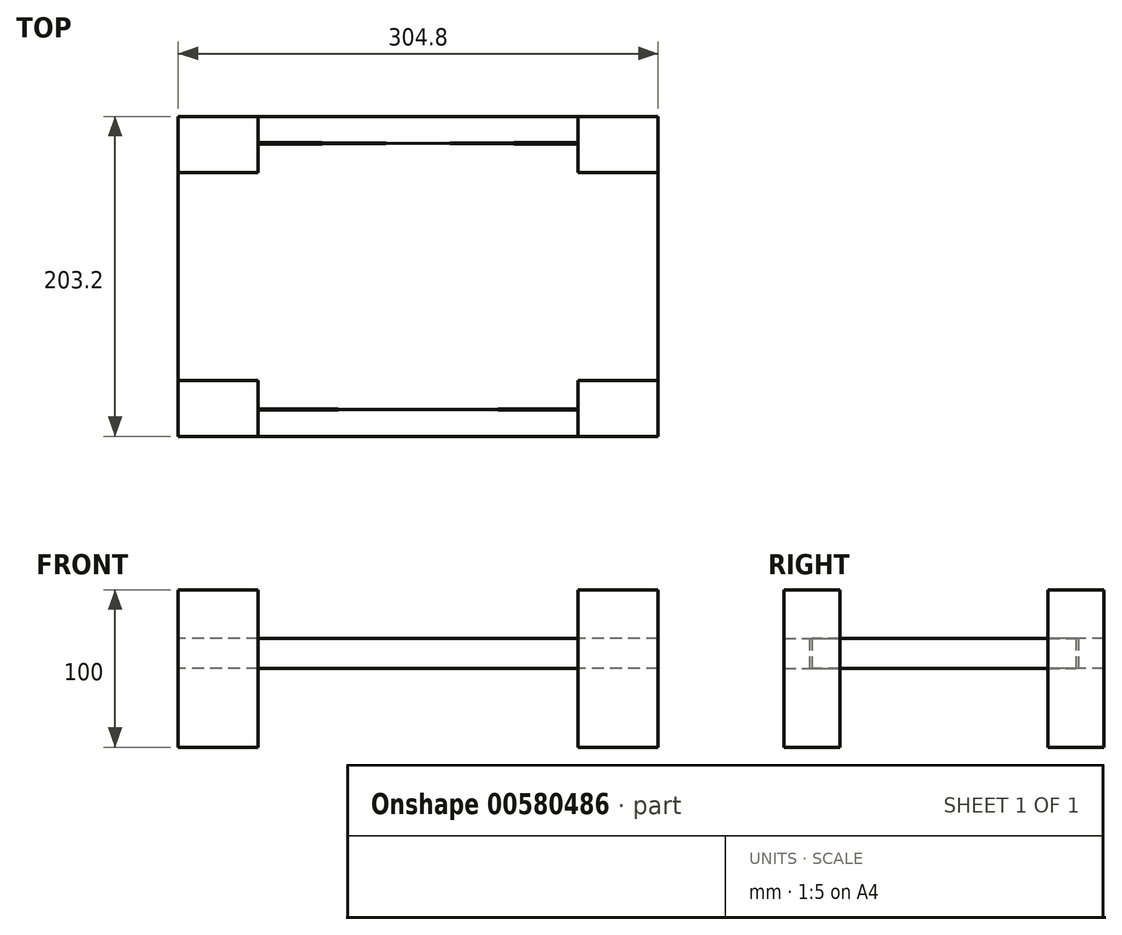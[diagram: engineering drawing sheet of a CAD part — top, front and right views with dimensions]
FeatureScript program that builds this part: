
annotation { "Feature Type Name" : "Feature", "Feature Type Description" : "" }
export const myFeature = defineFeature(function(context is Context, id is Id, definition is map)
    precondition{}
    {
        {
            var Q0;
            Q0=qCreatedBy(makeId("Top.planeOp"),FACE);
            var sketch = newSketch(context, id + "F0", { "sketchPlane" : qUnion([Q0])});
            skLineSegment(sketch, "E0.bottom", {"start": v(152.4, -101.6) * mm, "end": v(-152.4, -101.6) * mm});
            skLineSegment(sketch, "E0.top", {"start": v(152.4, 101.6) * mm, "end": v(-152.4, 101.6) * mm});
            skLineSegment(sketch, "E0.left", {"start": v(152.4, -101.6) * mm, "end": v(152.4, 101.6) * mm});
            skLineSegment(sketch, "E0.right", {"start": v(-152.4, -101.6) * mm, "end": v(-152.4, 101.6) * mm});
            skPoint(sketch, "E0.middle", {"position": v(0, 0) * mm});
            skLineSegment(sketch, "E1.bottom", {"start": v(152.4, -10.16) * mm, "end": v(-152.4, -10.16) * mm});
            skLineSegment(sketch, "E1.top", {"start": v(152.4, 10.16) * mm, "end": v(-152.4, 10.16) * mm});
            skLineSegment(sketch, "E1.left", {"start": v(152.4, -10.16) * mm, "end": v(152.4, 10.16) * mm});
            skLineSegment(sketch, "E1.right", {"start": v(-152.4, -10.16) * mm, "end": v(-152.4, 10.16) * mm});
            skLineSegment(sketch, "E2.bottom", {"start": v(-152.4, 101.6) * mm, "end": v(-101.6, 101.6) * mm});
            skLineSegment(sketch, "E2.top", {"start": v(-152.4, 66.04) * mm, "end": v(-101.6, 66.04) * mm});
            skLineSegment(sketch, "E2.left", {"start": v(-152.4, 101.6) * mm, "end": v(-152.4, 66.04) * mm});
            skLineSegment(sketch, "E2.right", {"start": v(-101.6, 101.6) * mm, "end": v(-101.6, 66.04) * mm});
            skLineSegment(sketch, "E3.MirrorCS", {"start": v(101.6, 101.6) * mm, "end": v(101.6, 66.04) * mm});
            skLineSegment(sketch, "E4.MirrorCS", {"start": v(152.4, 101.6) * mm, "end": v(152.4, 66.04) * mm});
            skLineSegment(sketch, "E5.MirrorCS", {"start": v(152.4, 66.04) * mm, "end": v(101.6, 66.04) * mm});
            skLineSegment(sketch, "E6.MirrorCS", {"start": v(152.4, 101.6) * mm, "end": v(101.6, 101.6) * mm});
            skLineSegment(sketch, "E7.MirrorCS", {"start": v(101.6, -101.6) * mm, "end": v(101.6, -66.04) * mm});
            skLineSegment(sketch, "E8.MirrorCS", {"start": v(-101.6, -101.6) * mm, "end": v(-101.6, -66.04) * mm});
            skLineSegment(sketch, "E9.MirrorCS", {"start": v(-152.4, -101.6) * mm, "end": v(-152.4, -66.04) * mm});
            skLineSegment(sketch, "E10.MirrorCS", {"start": v(-152.4, -66.04) * mm, "end": v(-101.6, -66.04) * mm});
            skLineSegment(sketch, "E11.MirrorCS", {"start": v(152.4, -101.6) * mm, "end": v(152.4, -66.04) * mm});
            skLineSegment(sketch, "E12.MirrorCS", {"start": v(-152.4, -101.6) * mm, "end": v(-101.6, -101.6) * mm});
            skLineSegment(sketch, "E13.MirrorCS", {"start": v(152.4, -66.04) * mm, "end": v(101.6, -66.04) * mm});
            skLineSegment(sketch, "E14.MirrorCS", {"start": v(152.4, -101.6) * mm, "end": v(101.6, -101.6) * mm});
            skLineSegment(sketch, "E15.bottom", {"start": v(-101.6, 101.6) * mm, "end": v(101.6, 101.6) * mm});
            skLineSegment(sketch, "E15.top", {"start": v(-101.6, 85.34) * mm, "end": v(101.6, 83.82) * mm});
            skLineSegment(sketch, "E15.left", {"start": v(-101.6, 101.6) * mm, "end": v(-101.6, 85.34) * mm});
            skLineSegment(sketch, "E15.right", {"start": v(101.6, 101.6) * mm, "end": v(101.6, 83.82) * mm});
            skLineSegment(sketch, "E16.MirrorCS", {"start": v(-101.6, -85.34) * mm, "end": v(101.6, -83.82) * mm});
            skSolve(sketch);
        }
        {
            var Q0;
            Q0=makeQuery(id+"F0.imprint","IMPRINT",FACE,{"disambiguationData":[TD([[makeQuery(id+"F0.imprint","IMPRINT",EDGE,{"derivedFrom":sQuery(id+"F0.wireOp",EDGE,"E1.bottom")}),-1.0]])]});
            var Q1;
            {var subQ1=sQuery(id+"F0.wireOp",EDGE,"E1.top");Q1=makeQuery(id+"F0.imprint","IMPRINT",FACE,{"disambiguationData":[TD([[makeQuery(id+"F0.imprint","IMPRINT",EDGE,{"derivedFrom":subQ1}),-1.0]])]});}
            var Q2;
            {var subQ3=sQuery(id+"F0.wireOp",EDGE,"E16.MirrorCS");Q2=makeQuery(id+"F0.imprint","IMPRINT",FACE,{"disambiguationData":[TD([[makeQuery(id+"F0.imprint","IMPRINT",EDGE,{"derivedFrom":subQ3}),-1.0]])]});}
            var Q3;
            Q3=makeQuery(id+"F0.imprint","IMPRINT",FACE,{"disambiguationData":[TD([[makeQuery(id+"F0.imprint","IMPRINT",EDGE,{"derivedFrom":sQuery(id+"F0.wireOp",EDGE,"E15.bottom")}),-1.0]])]});
            var Q4;
            {var subQ0=sQuery(id+"F0.wireOp",EDGE,"E1.bottom");Q4=makeQuery(id+"F0.imprint","IMPRINT",FACE,{"disambiguationData":[TD([[makeQuery(id+"F0.imprint","IMPRINT",EDGE,{"derivedFrom":subQ0}),1.0]])]});}
            var Q5;
            Q5=makeQuery(id+"F0.imprint","IMPRINT",FACE,{"disambiguationData":[TD([[makeQuery(id+"F0.imprint","IMPRINT",EDGE,{"derivedFrom":sQuery(id+"F0.wireOp",EDGE,"E2.bottom")}),-1.0]])]});
            var Q6;
            {var subQ1=sQuery(id+"F0.wireOp",EDGE,"E9.MirrorCS");Q6=makeQuery(id+"F0.imprint","IMPRINT",FACE,{"disambiguationData":[TD([[makeQuery(id+"F0.imprint","IMPRINT",EDGE,{"derivedFrom":subQ1}),-1.0]])]});}
            var Q7;
            {var subQ1=sQuery(id+"F0.wireOp",EDGE,"E11.MirrorCS");Q7=makeQuery(id+"F0.imprint","IMPRINT",FACE,{"disambiguationData":[TD([[makeQuery(id+"F0.imprint","IMPRINT",EDGE,{"derivedFrom":subQ1}),1.0]])]});}
            var Q8;
            Q8=makeQuery(id+"F0.imprint","IMPRINT",FACE,{"disambiguationData":[TD([[makeQuery(id+"F0.imprint","IMPRINT",EDGE,{"derivedFrom":sQuery(id+"F0.wireOp",EDGE,"E3.MirrorCS")}),1.0]])]});
            extrude(context, id + "F1", {"entities" : qUnion([Q0, Q1, Q2, Q3, Q4, Q5, Q6, Q7, Q8]), "depth" : 19.05 * mm, "offsetDistance" : 25 * mm});
        }
        {
            var Q0;
            {var subQ0=sQuery(id+"F0.wireOp",EDGE,"E8.MirrorCS");Q0=makeQuery(id+"F0.imprint","IMPRINT",FACE,{"disambiguationData":[TD([[makeQuery(id+"F0.imprint","IMPRINT",EDGE,{"derivedFrom":subQ0}),1.0]])]});}
            var Q1;
            Q1=makeQuery(id+"F0.imprint","IMPRINT",FACE,{"disambiguationData":[TD([[makeQuery(id+"F0.imprint","IMPRINT",EDGE,{"derivedFrom":sQuery(id+"F0.wireOp",EDGE,"E2.bottom")}),-1.0]])]});
            var Q2;
            Q2=makeQuery(id+"F0.imprint","IMPRINT",FACE,{"disambiguationData":[TD([[makeQuery(id+"F0.imprint","IMPRINT",EDGE,{"derivedFrom":sQuery(id+"F0.wireOp",EDGE,"E3.MirrorCS")}),1.0]])]});
            var Q3;
            {var subQ0=sQuery(id+"F0.wireOp",EDGE,"E7.MirrorCS");Q3=makeQuery(id+"F0.imprint","IMPRINT",FACE,{"disambiguationData":[TD([[makeQuery(id+"F0.imprint","IMPRINT",EDGE,{"derivedFrom":subQ0}),-1.0]])]});}
            extrude(context, id + "F2", {"entities" : qUnion([Q0, Q1, Q2, Q3]), "operationType" : NewBodyOperationType.ADD, "endBound" : BoundingType.SYMMETRIC, "depth" : 100 * mm, "offsetDistance" : 25 * mm});
        }
        {
            var Q0;
            Q0=qCreatedBy(makeId("Front.planeOp"),FACE);
            var sketch = newSketch(context, id + "F3", { "sketchPlane" : qUnion([Q0])});
            skArc(sketch, "E17", {"start": v(65.86, -29.73) * mm, "mid": v(0.22, -1.4) * mm, "end": v(-65.49, -29.56) * mm});
            skArc(sketch, "E18.0", {"start": v(68.77, -26.98) * mm, "mid": v(0.23, 2.6) * mm, "end": v(-68.39, -26.8) * mm});
            skLineSegment(sketch, "E19", {"start": v(68.77, -26.98) * mm, "end": v(65.86, -29.73) * mm});
            skLineSegment(sketch, "E20", {"start": v(-65.49, -29.56) * mm, "end": v(-68.39, -26.8) * mm});
            skSolve(sketch);
        }
        {
            var Q0;
            {var subQ1=sQuery(id+"F0.wireOp",EDGE,"E1.bottom");Q0=makeQuery(id+"F0.imprint","IMPRINT",FACE,{"disambiguationData":[TD([[makeQuery(id+"F0.imprint","IMPRINT",EDGE,{"derivedFrom":subQ1}),1.0]])]});}
            var sketch = newSketch(context, id + "F4", { "sketchPlane" : qUnion([Q0])});
            skLineSegment(sketch, "E21.bottom", {"start": v(-61.68, -101.6) * mm, "end": v(-60.58, -101.6) * mm});
            skLineSegment(sketch, "E21.top", {"start": v(-61.68, 101.6) * mm, "end": v(-60.58, 101.6) * mm});
            skLineSegment(sketch, "E21.left", {"start": v(-61.68, -101.6) * mm, "end": v(-61.68, 101.6) * mm});
            skLineSegment(sketch, "E21.right", {"start": v(-60.58, -101.6) * mm, "end": v(-60.58, 101.6) * mm});
            skLineSegment(sketch, "E22.1.0.0", {"start": v(-53.68, -101.6) * mm, "end": v(-53.68, 101.6) * mm});
            skLineSegment(sketch, "E22.1.0.1", {"start": v(-52.58, -101.6) * mm, "end": v(-52.58, 101.6) * mm});
            skLineSegment(sketch, "E22.1.0.2", {"start": v(-53.68, -101.6) * mm, "end": v(-52.58, -101.6) * mm});
            skLineSegment(sketch, "E22.1.0.3", {"start": v(-53.68, 101.6) * mm, "end": v(-52.58, 101.6) * mm});
            skLineSegment(sketch, "E22.2.0.0", {"start": v(-45.68, -101.6) * mm, "end": v(-45.68, 101.6) * mm});
            skLineSegment(sketch, "E22.2.0.1", {"start": v(-44.58, -101.6) * mm, "end": v(-44.58, 101.6) * mm});
            skLineSegment(sketch, "E22.2.0.2", {"start": v(-45.68, -101.6) * mm, "end": v(-44.58, -101.6) * mm});
            skLineSegment(sketch, "E22.2.0.3", {"start": v(-45.68, 101.6) * mm, "end": v(-44.58, 101.6) * mm});
            skLineSegment(sketch, "E22.3.0.0", {"start": v(-37.68, -101.6) * mm, "end": v(-37.68, 101.6) * mm});
            skLineSegment(sketch, "E22.3.0.1", {"start": v(-36.58, -101.6) * mm, "end": v(-36.58, 101.6) * mm});
            skLineSegment(sketch, "E22.3.0.2", {"start": v(-37.68, -101.6) * mm, "end": v(-36.58, -101.6) * mm});
            skLineSegment(sketch, "E22.3.0.3", {"start": v(-37.68, 101.6) * mm, "end": v(-36.58, 101.6) * mm});
            skLineSegment(sketch, "E22.4.0.0", {"start": v(-29.68, -101.6) * mm, "end": v(-29.68, 101.6) * mm});
            skLineSegment(sketch, "E22.4.0.1", {"start": v(-28.58, -101.6) * mm, "end": v(-28.58, 101.6) * mm});
            skLineSegment(sketch, "E22.4.0.2", {"start": v(-29.68, -101.6) * mm, "end": v(-28.58, -101.6) * mm});
            skLineSegment(sketch, "E22.4.0.3", {"start": v(-29.68, 101.6) * mm, "end": v(-28.58, 101.6) * mm});
            skLineSegment(sketch, "E22.5.0.0", {"start": v(-21.68, -101.6) * mm, "end": v(-21.68, 101.6) * mm});
            skLineSegment(sketch, "E22.5.0.1", {"start": v(-20.58, -101.6) * mm, "end": v(-20.58, 101.6) * mm});
            skLineSegment(sketch, "E22.5.0.2", {"start": v(-21.68, -101.6) * mm, "end": v(-20.58, -101.6) * mm});
            skLineSegment(sketch, "E22.5.0.3", {"start": v(-21.68, 101.6) * mm, "end": v(-20.58, 101.6) * mm});
            skLineSegment(sketch, "E22.direction1", {"start": v(-61.68, -101.6) * mm, "end": v(-53.68, -101.6) * mm, "construction": true});
            skLineSegment(sketch, "E23.MirrorCS", {"start": v(53.68, -101.6) * mm, "end": v(52.58, -101.6) * mm});
            skLineSegment(sketch, "E24.MirrorCS", {"start": v(61.68, -101.6) * mm, "end": v(60.58, -101.6) * mm});
            skLineSegment(sketch, "E25.MirrorCS", {"start": v(53.68, 101.6) * mm, "end": v(52.58, 101.6) * mm});
            skLineSegment(sketch, "E26.MirrorCS", {"start": v(61.68, 101.6) * mm, "end": v(60.58, 101.6) * mm});
            skLineSegment(sketch, "E27.MirrorCS", {"start": v(37.68, 101.6) * mm, "end": v(36.58, 101.6) * mm});
            skLineSegment(sketch, "E28.MirrorCS", {"start": v(37.68, -101.6) * mm, "end": v(36.58, -101.6) * mm});
            skLineSegment(sketch, "E29.MirrorCS", {"start": v(29.68, 101.6) * mm, "end": v(28.58, 101.6) * mm});
            skLineSegment(sketch, "E30.MirrorCS", {"start": v(29.68, -101.6) * mm, "end": v(28.58, -101.6) * mm});
            skLineSegment(sketch, "E31.MirrorCS", {"start": v(21.68, -101.6) * mm, "end": v(20.58, -101.6) * mm});
            skLineSegment(sketch, "E32.MirrorCS", {"start": v(21.68, 101.6) * mm, "end": v(20.58, 101.6) * mm});
            skLineSegment(sketch, "E33.MirrorCS", {"start": v(45.68, -101.6) * mm, "end": v(44.58, -101.6) * mm});
            skLineSegment(sketch, "E34.MirrorCS", {"start": v(45.68, 101.6) * mm, "end": v(44.58, 101.6) * mm});
            skLineSegment(sketch, "E35.MirrorCS", {"start": v(45.68, -101.6) * mm, "end": v(45.68, 101.6) * mm});
            skLineSegment(sketch, "E36.MirrorCS", {"start": v(44.58, -101.6) * mm, "end": v(44.58, 101.6) * mm});
            skLineSegment(sketch, "E37.MirrorCS", {"start": v(52.58, -101.6) * mm, "end": v(52.58, 101.6) * mm});
            skLineSegment(sketch, "E38.MirrorCS", {"start": v(53.68, -101.6) * mm, "end": v(53.68, 101.6) * mm});
            skLineSegment(sketch, "E39.MirrorCS", {"start": v(60.58, -101.6) * mm, "end": v(60.58, 101.6) * mm});
            skLineSegment(sketch, "E40.MirrorCS", {"start": v(61.68, -101.6) * mm, "end": v(61.68, 101.6) * mm});
            skLineSegment(sketch, "E41.MirrorCS", {"start": v(36.58, -101.6) * mm, "end": v(36.58, 101.6) * mm});
            skLineSegment(sketch, "E42.MirrorCS", {"start": v(61.68, -101.6) * mm, "end": v(53.68, -101.6) * mm, "construction": true});
            skLineSegment(sketch, "E43.MirrorCS", {"start": v(20.58, -101.6) * mm, "end": v(20.58, 101.6) * mm});
            skLineSegment(sketch, "E44.MirrorCS", {"start": v(28.58, -101.6) * mm, "end": v(28.58, 101.6) * mm});
            skLineSegment(sketch, "E45.MirrorCS", {"start": v(21.68, -101.6) * mm, "end": v(21.68, 101.6) * mm});
            skLineSegment(sketch, "E46.MirrorCS", {"start": v(29.68, -101.6) * mm, "end": v(29.68, 101.6) * mm});
            skLineSegment(sketch, "E47.MirrorCS", {"start": v(37.68, -101.6) * mm, "end": v(37.68, 101.6) * mm});
            skSolve(sketch);
        }
        {
            var Q0;
            {var subQ0=sQuery(id+"F0.wireOp",EDGE,"E16.MirrorCS");var subQ3=sQuery(id+"F0.wireOp",EDGE,"E7.MirrorCS");Q0=makeQuery(id+"F2.boolean.opBoolean","SPLIT",FACE,{"disambiguationData":[TD([makeQuery(id+"FBi03Cy3b78UQKm_1.opExtrude","SWEPT_FACE",FACE,{"disambiguationData":[OSD([subQ0])]})])],"derivedFrom":makeQuery(id+"F2.opExtrude","SWEPT_FACE",FACE,{"disambiguationData":[OSD([subQ3])]})});}
            var sketch = newSketch(context, id + "F5", { "sketchPlane" : qUnion([Q0])});
            skCircle(sketch, "E48", {"center": v(17.8, 27.68) * mm, "radius": 1.14 * mm});
            skCircle(sketch, "E49.1.0.0", {"center": v(17.8, 23.68) * mm, "radius": 1.14 * mm});
            skCircle(sketch, "E49.2.0.0", {"center": v(17.8, 19.68) * mm, "radius": 1.14 * mm});
            skLineSegment(sketch, "E49.direction1", {"start": v(17.8, 27.68) * mm, "end": v(17.8, 23.68) * mm, "construction": true});
            skSolve(sketch);
        }
        {
            var Q0;
            Q0=makeQuery(id+"FBi03Cy3b78UQKm_1.opExtrude","CAP_FACE",FACE,{"disambiguationData":[OSD([sQuery(id+"F0.wireOp",EDGE,"E7.MirrorCS"),sQuery(id+"F0.wireOp",EDGE,"E8.MirrorCS"),sQuery(id+"F0.wireOp",EDGE,"E0.bottom"),sQuery(id+"F0.wireOp",EDGE,"E16.MirrorCS")])],"isStart":false});
            var sketch = newSketch(context, id + "F6", { "sketchPlane" : qUnion([Q0])});
            skCircle(sketch, "E50", {"center": v(50.54, -19.06) * mm, "radius": 0.8 * mm});
            skCircle(sketch, "E51.1.0.0", {"center": v(46.54, -19.1) * mm, "radius": 0.8 * mm});
            skCircle(sketch, "E51.2.0.0", {"center": v(42.54, -19.14) * mm, "radius": 0.8 * mm});
            skLineSegment(sketch, "E51.direction1", {"start": v(50.54, -19.06) * mm, "end": v(46.54, -19.1) * mm, "construction": true});
            skSolve(sketch);
        }
        {
            var Q0;
            Q0=makeQuery(id+"FRw2Enb5HnM0TXF_1.opLoft","SWEPT_BODY",BODY,{"disambiguationData":[OSD([makeQuery(id+"F5.imprint","IMPRINT",FACE,{"disambiguationData":[TD([[makeQuery(id+"F5.imprint","IMPRINT",EDGE,{"derivedFrom":sQuery(id+"F5.wireOp",EDGE,"E49.1.0.0")}),1.0]])]}),makeQuery(id+"F6.imprint","IMPRINT",FACE,{"disambiguationData":[TD([[makeQuery(id+"F6.imprint","IMPRINT",EDGE,{"derivedFrom":sQuery(id+"F6.wireOp",EDGE,"E51.1.0.0")}),1.0]])]})])]});
            var Q1;
            Q1=makeQuery(id+"FHDKQl6653cWzUJ_2.opLoft","SWEPT_BODY",BODY,{"disambiguationData":[OSD([makeQuery(id+"F5.imprint","IMPRINT",FACE,{"disambiguationData":[TD([[makeQuery(id+"F5.imprint","IMPRINT",EDGE,{"derivedFrom":sQuery(id+"F5.wireOp",EDGE,"E49.2.0.0")}),1.0]])]}),makeQuery(id+"F6.imprint","IMPRINT",FACE,{"disambiguationData":[TD([[makeQuery(id+"F6.imprint","IMPRINT",EDGE,{"derivedFrom":sQuery(id+"F6.wireOp",EDGE,"E50")}),1.0]])]})])]});
            var Q2;
            Q2=makeQuery(id+"F1.opExtrude","SWEPT_BODY",BODY,{"disambiguationData":[OSD([sQuery(id+"F0.wireOp",EDGE,"E0.left"),sQuery(id+"F0.wireOp",EDGE,"E0.right"),sQuery(id+"F0.wireOp",EDGE,"E1.left"),sQuery(id+"F0.wireOp",EDGE,"E1.right"),sQuery(id+"F0.wireOp",EDGE,"E2.bottom"),sQuery(id+"F0.wireOp",EDGE,"E2.left"),sQuery(id+"F0.wireOp",EDGE,"E4.MirrorCS"),sQuery(id+"F0.wireOp",EDGE,"E6.MirrorCS"),sQuery(id+"F0.wireOp",EDGE,"E9.MirrorCS"),sQuery(id+"F0.wireOp",EDGE,"E11.MirrorCS"),sQuery(id+"F0.wireOp",EDGE,"E0.bottom"),sQuery(id+"F0.wireOp",EDGE,"E15.bottom")])]});
            var Q3;
            Q3=qCreatedBy(makeId("Front.planeOp"),FACE);
            mirror(context, id + "F7", {"entities" : qUnion([Q0, Q1, Q2]), "mirrorPlane" : qUnion([Q3])});
        }
        {
            var Q0;
            Q0=makeQuery(id+"FRw2Enb5HnM0TXF_1.opLoft","SWEPT_BODY",BODY,{"disambiguationData":[OSD([makeQuery(id+"F5.imprint","IMPRINT",FACE,{"disambiguationData":[TD([[makeQuery(id+"F5.imprint","IMPRINT",EDGE,{"derivedFrom":sQuery(id+"F5.wireOp",EDGE,"E49.1.0.0")}),1.0]])]}),makeQuery(id+"F6.imprint","IMPRINT",FACE,{"disambiguationData":[TD([[makeQuery(id+"F6.imprint","IMPRINT",EDGE,{"derivedFrom":sQuery(id+"F6.wireOp",EDGE,"E51.1.0.0")}),1.0]])]})])]});
            var Q1;
            Q1=makeQuery(id+"FHDKQl6653cWzUJ_2.opLoft","SWEPT_BODY",BODY,{"disambiguationData":[OSD([makeQuery(id+"F5.imprint","IMPRINT",FACE,{"disambiguationData":[TD([[makeQuery(id+"F5.imprint","IMPRINT",EDGE,{"derivedFrom":sQuery(id+"F5.wireOp",EDGE,"E49.2.0.0")}),1.0]])]}),makeQuery(id+"F6.imprint","IMPRINT",FACE,{"disambiguationData":[TD([[makeQuery(id+"F6.imprint","IMPRINT",EDGE,{"derivedFrom":sQuery(id+"F6.wireOp",EDGE,"E50")}),1.0]])]})])]});
            var Q2;
            Q2=makeQuery(id+"F7.opPattern","COPY",BODY,{"derivedFrom":makeQuery(id+"F1.opExtrude","SWEPT_BODY",BODY,{"disambiguationData":[OSD([sQuery(id+"F0.wireOp",EDGE,"E0.left"),sQuery(id+"F0.wireOp",EDGE,"E0.right"),sQuery(id+"F0.wireOp",EDGE,"E1.left"),sQuery(id+"F0.wireOp",EDGE,"E1.right"),sQuery(id+"F0.wireOp",EDGE,"E2.bottom"),sQuery(id+"F0.wireOp",EDGE,"E2.left"),sQuery(id+"F0.wireOp",EDGE,"E4.MirrorCS"),sQuery(id+"F0.wireOp",EDGE,"E6.MirrorCS"),sQuery(id+"F0.wireOp",EDGE,"E9.MirrorCS"),sQuery(id+"F0.wireOp",EDGE,"E11.MirrorCS"),sQuery(id+"F0.wireOp",EDGE,"E0.bottom"),sQuery(id+"F0.wireOp",EDGE,"E15.bottom")])]}),"instanceName":"1"});
            var Q3;
            Q3=makeQuery(id+"F7.opPattern","COPY",BODY,{"derivedFrom":makeQuery(id+"FRw2Enb5HnM0TXF_1.opLoft","SWEPT_BODY",BODY,{"disambiguationData":[OSD([makeQuery(id+"F5.imprint","IMPRINT",FACE,{"disambiguationData":[TD([[makeQuery(id+"F5.imprint","IMPRINT",EDGE,{"derivedFrom":sQuery(id+"F5.wireOp",EDGE,"E49.1.0.0")}),1.0]])]}),makeQuery(id+"F6.imprint","IMPRINT",FACE,{"disambiguationData":[TD([[makeQuery(id+"F6.imprint","IMPRINT",EDGE,{"derivedFrom":sQuery(id+"F6.wireOp",EDGE,"E51.1.0.0")}),1.0]])]})])]}),"instanceName":"1"});
            var Q4;
            Q4=makeQuery(id+"F7.opPattern","COPY",BODY,{"derivedFrom":makeQuery(id+"FHDKQl6653cWzUJ_2.opLoft","SWEPT_BODY",BODY,{"disambiguationData":[OSD([makeQuery(id+"F5.imprint","IMPRINT",FACE,{"disambiguationData":[TD([[makeQuery(id+"F5.imprint","IMPRINT",EDGE,{"derivedFrom":sQuery(id+"F5.wireOp",EDGE,"E49.2.0.0")}),1.0]])]}),makeQuery(id+"F6.imprint","IMPRINT",FACE,{"disambiguationData":[TD([[makeQuery(id+"F6.imprint","IMPRINT",EDGE,{"derivedFrom":sQuery(id+"F6.wireOp",EDGE,"E50")}),1.0]])]})])]}),"instanceName":"1"});
            var Q5;
            Q5=makeQuery(id+"F1.opExtrude","SWEPT_BODY",BODY,{"disambiguationData":[OSD([sQuery(id+"F0.wireOp",EDGE,"E0.left"),sQuery(id+"F0.wireOp",EDGE,"E0.right"),sQuery(id+"F0.wireOp",EDGE,"E1.left"),sQuery(id+"F0.wireOp",EDGE,"E1.right"),sQuery(id+"F0.wireOp",EDGE,"E2.bottom"),sQuery(id+"F0.wireOp",EDGE,"E2.left"),sQuery(id+"F0.wireOp",EDGE,"E4.MirrorCS"),sQuery(id+"F0.wireOp",EDGE,"E6.MirrorCS"),sQuery(id+"F0.wireOp",EDGE,"E9.MirrorCS"),sQuery(id+"F0.wireOp",EDGE,"E11.MirrorCS"),sQuery(id+"F0.wireOp",EDGE,"E0.bottom"),sQuery(id+"F0.wireOp",EDGE,"E15.bottom")])]});
            var Q6;
            Q6=qCreatedBy(makeId("Right.planeOp"),FACE);
            mirror(context, id + "F8", {"entities" : qUnion([Q0, Q1, Q2, Q3, Q4, Q5]), "mirrorPlane" : qUnion([Q6])});
        }
        {
            var Q0;
            {var subQ0=sQuery(id+"F0.wireOp",EDGE,"E0.bottom");Q0=makeQuery(id+"Ft0mDCr2Mikjukp_1.boolean.opBoolean","MERGE",FACE,{"derivedFrom":[makeQuery(id+"FNBR20YmUJhHsRu_1.boolean.opBoolean","MERGE",FACE,{"derivedFrom":[makeQuery(id+"F2.boolean.opBoolean","MERGE",FACE,{"derivedFrom":[makeQuery(id+"FBi03Cy3b78UQKm_1.boolean.opBoolean","MERGE",FACE,{"derivedFrom":[makeQuery(id+"F1.opExtrude","SWEPT_FACE",FACE,{"disambiguationData":[OSD([subQ0])]}),makeQuery(id+"FBi03Cy3b78UQKm_1.opExtrude","SWEPT_FACE",FACE,{"disambiguationData":[OSD([subQ0])]})]}),makeQuery(id+"F2.opExtrude","SWEPT_FACE",FACE,{"disambiguationData":[OSD([subQ0]),TDD([makeQuery(id+"F0.imprint","IMPRINT",EDGE,{"disambiguationData":[TD([[makeQuery(id+"F0.imprint","INTERSECT",VERTEX,{"derivedFrom":[sQuery(id+"F0.wireOp",EDGE,"E7.MirrorCS"),subQ0]}),1.0]])],"derivedFrom":subQ0})])]}),makeQuery(id+"F2.opExtrude","SWEPT_FACE",FACE,{"disambiguationData":[OSD([subQ0]),TDD([makeQuery(id+"F0.imprint","IMPRINT",EDGE,{"disambiguationData":[TD([[makeQuery(id+"F0.imprint","INTERSECT",VERTEX,{"derivedFrom":[sQuery(id+"F0.wireOp",EDGE,"E8.MirrorCS"),subQ0]}),-1.0]])],"derivedFrom":subQ0})])]})]}),makeQuery(id+"FNBR20YmUJhHsRu_1.opExtrude","CAP_FACE",FACE,{"disambiguationData":[OSD([sQuery(id+"F3.wireOp",EDGE,"E17"),sQuery(id+"F3.wireOp",EDGE,"E18.0"),sQuery(id+"F3.wireOp",EDGE,"E19"),sQuery(id+"F3.wireOp",EDGE,"E20")])],"isStart":false})]}),makeQuery(id+"Ft0mDCr2Mikjukp_1.opExtrude","SWEPT_FACE",FACE,{"disambiguationData":[OSD([sQuery(id+"F4.wireOp",EDGE,"E21.bottom")])]}),makeQuery(id+"Ft0mDCr2Mikjukp_1.opExtrude","SWEPT_FACE",FACE,{"disambiguationData":[OSD([sQuery(id+"F4.wireOp",EDGE,"E22.1.0.2")])]}),makeQuery(id+"Ft0mDCr2Mikjukp_1.opExtrude","SWEPT_FACE",FACE,{"disambiguationData":[OSD([sQuery(id+"F4.wireOp",EDGE,"E22.2.0.2")])]}),makeQuery(id+"Ft0mDCr2Mikjukp_1.opExtrude","SWEPT_FACE",FACE,{"disambiguationData":[OSD([sQuery(id+"F4.wireOp",EDGE,"E22.3.0.2")])]}),makeQuery(id+"Ft0mDCr2Mikjukp_1.opExtrude","SWEPT_FACE",FACE,{"disambiguationData":[OSD([sQuery(id+"F4.wireOp",EDGE,"E22.4.0.2")])]}),makeQuery(id+"Ft0mDCr2Mikjukp_1.opExtrude","SWEPT_FACE",FACE,{"disambiguationData":[OSD([sQuery(id+"F4.wireOp",EDGE,"E23.MirrorCS")])]}),makeQuery(id+"Ft0mDCr2Mikjukp_1.opExtrude","SWEPT_FACE",FACE,{"disambiguationData":[OSD([sQuery(id+"F4.wireOp",EDGE,"E24.MirrorCS")])]}),makeQuery(id+"Ft0mDCr2Mikjukp_1.opExtrude","SWEPT_FACE",FACE,{"disambiguationData":[OSD([sQuery(id+"F4.wireOp",EDGE,"E28.MirrorCS")])]}),makeQuery(id+"Ft0mDCr2Mikjukp_1.opExtrude","SWEPT_FACE",FACE,{"disambiguationData":[OSD([sQuery(id+"F4.wireOp",EDGE,"E30.MirrorCS")])]}),makeQuery(id+"Ft0mDCr2Mikjukp_1.opExtrude","SWEPT_FACE",FACE,{"disambiguationData":[OSD([sQuery(id+"F4.wireOp",EDGE,"E33.MirrorCS")])]})]});}
            var sketch = newSketch(context, id + "F9", { "sketchPlane" : qUnion([Q0])});
            skLineSegment(sketch, "E52", {"start": v(-64.93, 19.24) * mm, "end": v(71.83, 19.24) * mm});
            skArc(sketch, "E53", {"start": v(-28.7, 19.24) * mm, "mid": v(-46.8, 32.32) * mm, "end": v(-64.93, 19.24) * mm});
            skArc(sketch, "E54", {"start": v(11.05, 19.24) * mm, "mid": v(-7.4, 32.14) * mm, "end": v(-25.85, 19.24) * mm});
            skArc(sketch, "E55", {"start": v(48.68, 19.24) * mm, "mid": v(31.7, 31.11) * mm, "end": v(14.74, 19.24) * mm});
            skArc(sketch, "E56", {"start": v(71.83, 19.24) * mm, "mid": v(61.2, 30.3) * mm, "end": v(50.55, 19.24) * mm});
            skLineSegment(sketch, "E57", {"start": v(71.83, 19.24) * mm, "end": v(-64.93, 19.24) * mm});
            skSolve(sketch);
        }
        {
            var Q0;
            Q0=qSketchRegion(id+"F9",true);
            extrude(context, id + "F10", {"entities" : qUnion([Q0]), "operationType" : NewBodyOperationType.REMOVE, "oppositeDirection" : true, "depth" : 79.4 * mm, "offsetDistance" : 25 * mm});
        }
    });
